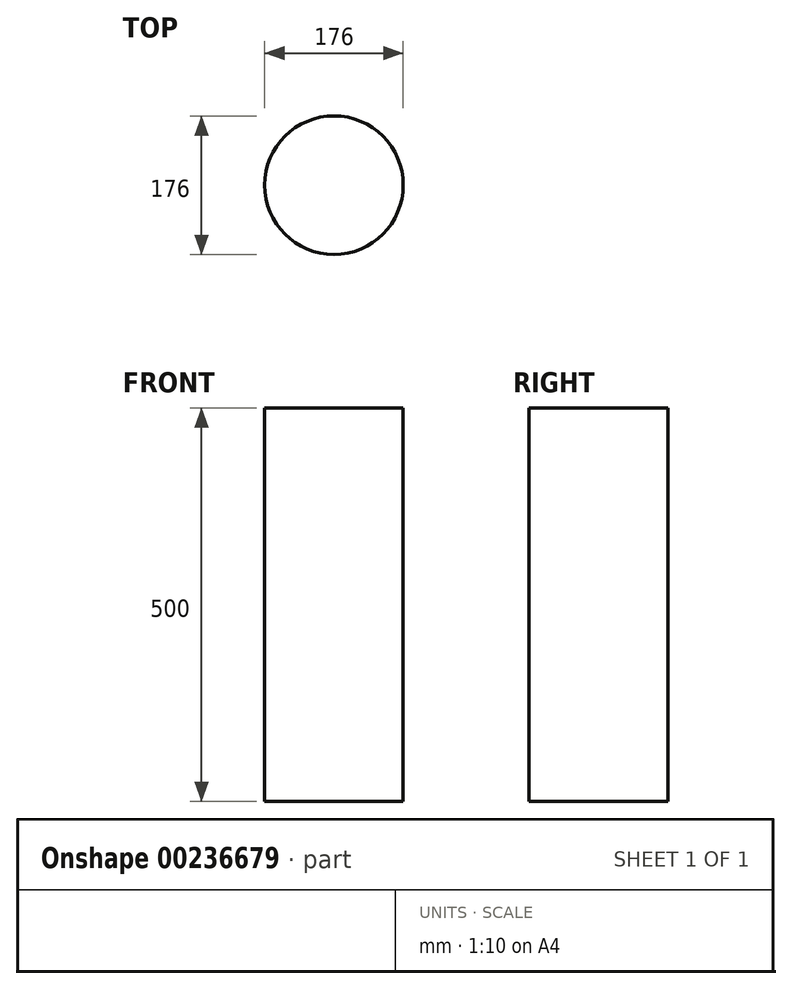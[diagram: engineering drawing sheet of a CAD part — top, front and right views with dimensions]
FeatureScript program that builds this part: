
annotation { "Feature Type Name" : "Feature", "Feature Type Description" : "" }
export const myFeature = defineFeature(function(context is Context, id is Id, definition is map)
    precondition{}
    {
        {
            var Q0;
            Q0=qCreatedBy(makeId("Top.planeOp"),FACE);
            var sketch = newSketch(context, id + "F0", { "sketchPlane" : qUnion([Q0])});
            skCircle(sketch, "E0", {"center": v(0, 0) * mm, "radius": 88 * mm});
            skSolve(sketch);
        }
        {
            var Q0;
            Q0 = qSketchRegion(id + "F0", true);
            extrude(context, id + "F1", {"entities" : qUnion([Q0]), "depth" : 500 * mm});
        }
    });
